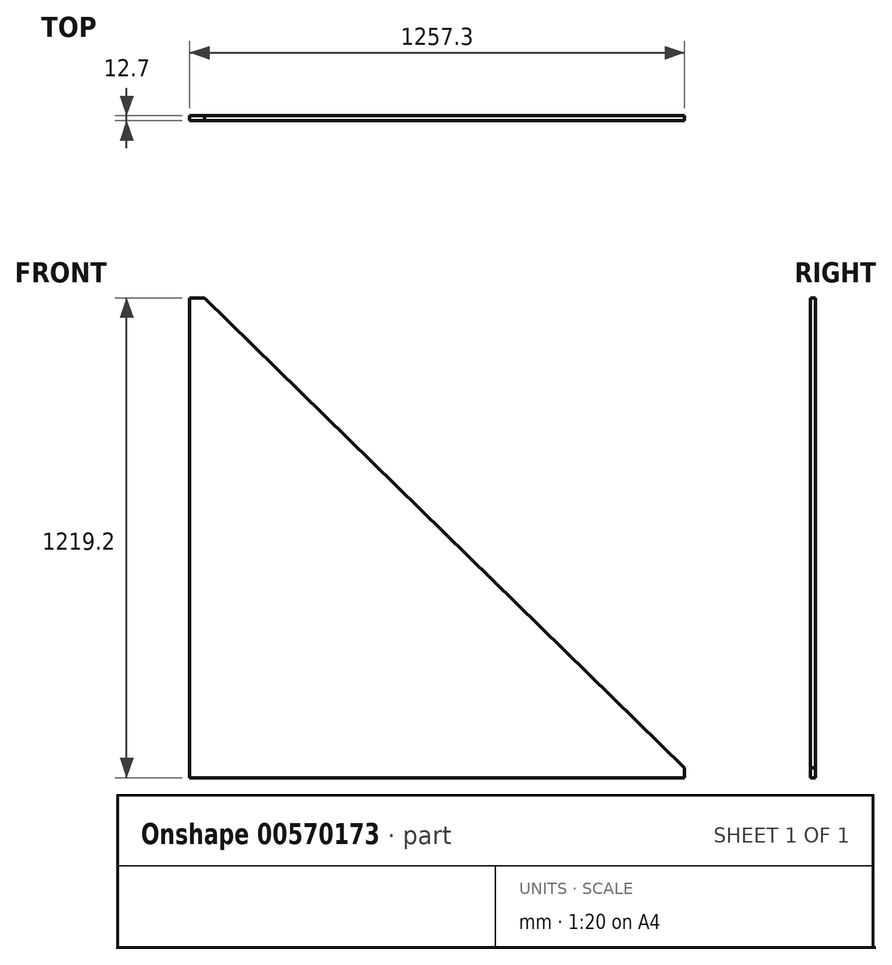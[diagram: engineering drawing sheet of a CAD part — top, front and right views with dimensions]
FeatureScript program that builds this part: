
annotation { "Feature Type Name" : "Feature", "Feature Type Description" : "" }
export const myFeature = defineFeature(function(context is Context, id is Id, definition is map)
    precondition{}
    {
        {
            var Q0;
            Q0=qCreatedBy(makeId("Front.planeOp"),FACE);
            var sketch = newSketch(context, id + "F0", { "sketchPlane" : qUnion([Q0])});
            skLineSegment(sketch, "E0", {"start": v(0, 0) * mm, "end": v(0, 1219.2) * mm});
            skLineSegment(sketch, "E1", {"start": v(0, 1219.2) * mm, "end": v(38.1, 1219.2) * mm});
            skLineSegment(sketch, "E2", {"start": v(38.1, 1219.2) * mm, "end": v(1257.3, 25.4) * mm});
            skLineSegment(sketch, "E3", {"start": v(1257.3, 25.4) * mm, "end": v(1257.3, 0) * mm});
            skLineSegment(sketch, "E4", {"start": v(1257.3, 0) * mm, "end": v(0, 0) * mm});
            skSolve(sketch);
        }
        {
            var Q0;
            Q0 = qSketchRegion(id + "F0", true);
            extrude(context, id + "F1", {"entities" : qUnion([Q0]), "depth" : 12.7 * mm, "offsetDistance" : 25.4 * mm});
        }
    });
